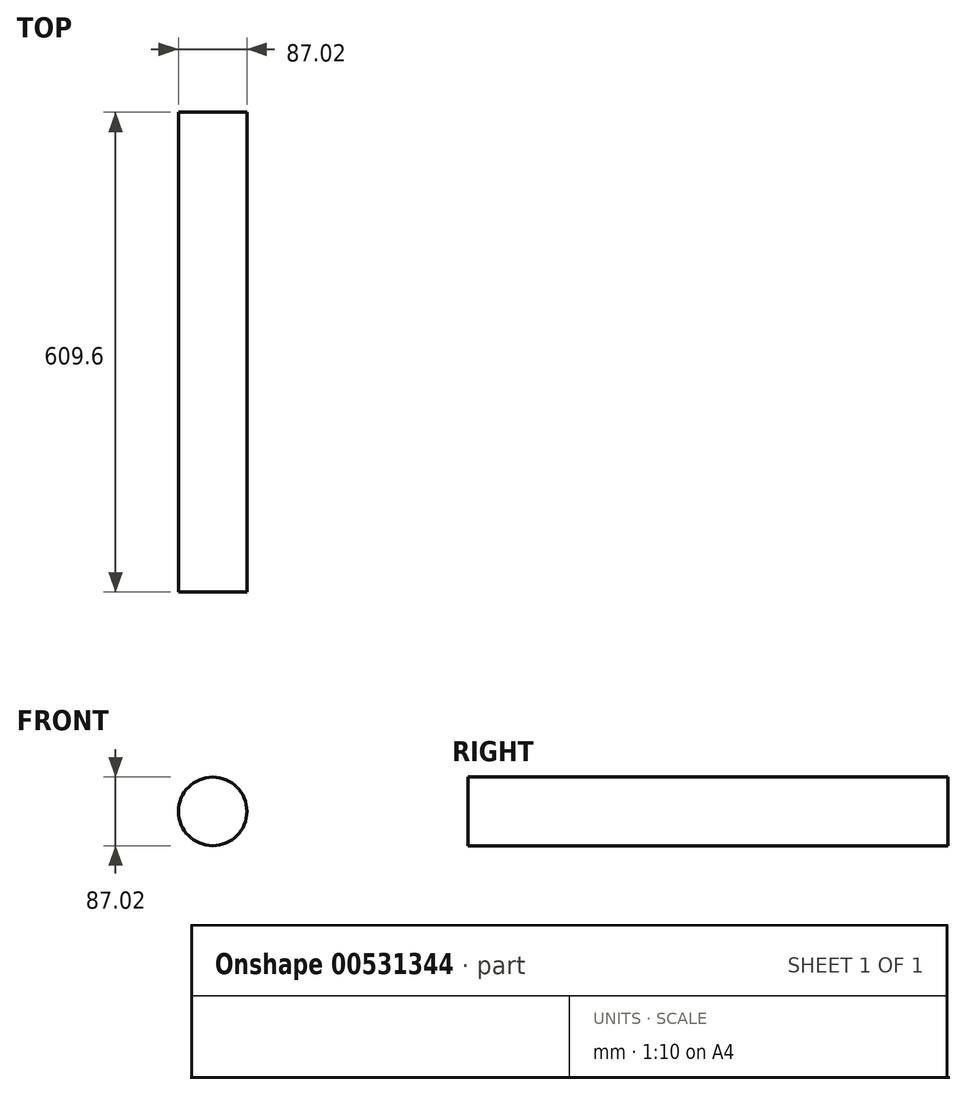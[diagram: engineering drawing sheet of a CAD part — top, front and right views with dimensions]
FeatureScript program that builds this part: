
annotation { "Feature Type Name" : "Feature", "Feature Type Description" : "" }
export const myFeature = defineFeature(function(context is Context, id is Id, definition is map)
    precondition{}
    {
        {
            var Q0;
            Q0=qCreatedBy(makeId("Front.planeOp"),FACE);
            var sketch = newSketch(context, id + "F0", { "sketchPlane" : qUnion([Q0])});
            skCircle(sketch, "E0", {"center": v(-68.98, 16.87) * mm, "radius": 43.5 * mm});
            skSolve(sketch);
        }
        {
            var Q0;
            Q0 = qSketchRegion(id + "F0", true);
            extrude(context, id + "F1", {"entities" : qUnion([Q0]), "depth" : 609.6 * mm, "offsetDistance" : 25.4 * mm});
        }
    });
